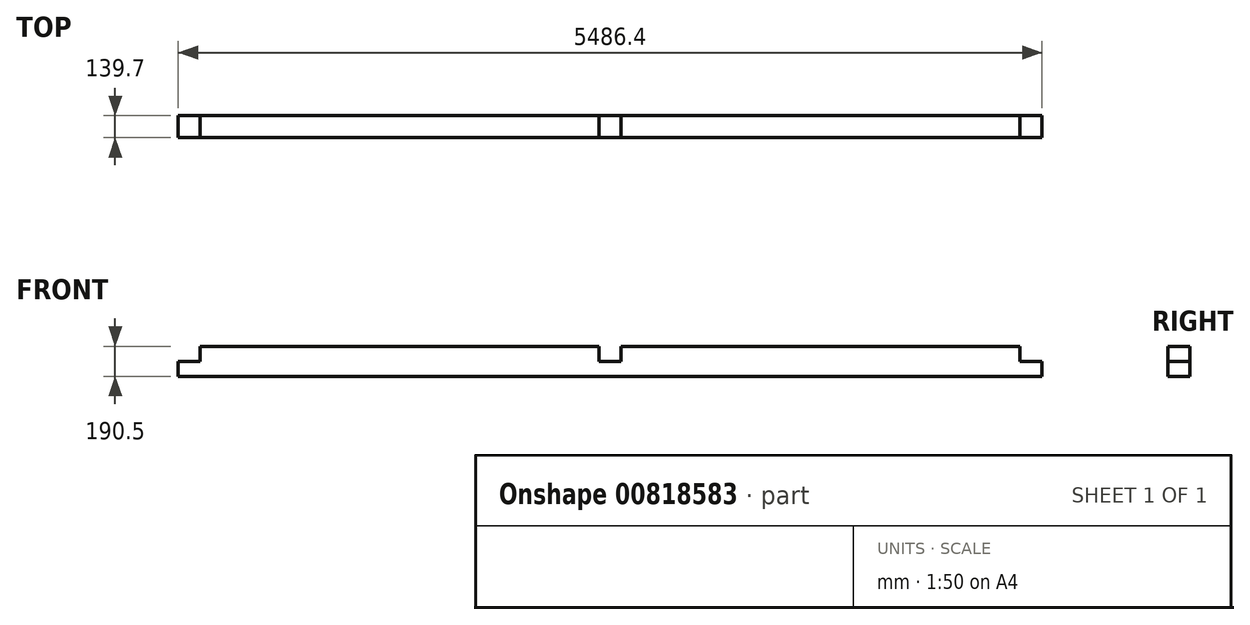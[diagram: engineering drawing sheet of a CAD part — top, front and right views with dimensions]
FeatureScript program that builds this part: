
annotation { "Feature Type Name" : "Feature", "Feature Type Description" : "" }
export const myFeature = defineFeature(function(context is Context, id is Id, definition is map)
    precondition{}
    {
        {
            var Q0;
            Q0=qCreatedBy(makeId("Front.planeOp"),FACE);
            var sketch = newSketch(context, id + "F0", { "sketchPlane" : qUnion([Q0])});
            skLineSegment(sketch, "E0.bottom", {"start": v(181.14, -116.54) * mm, "end": v(2924.34, -116.54) * mm});
            skLineSegment(sketch, "E0.top", {"start": v(181.14, 73.96) * mm, "end": v(5667.54, 73.96) * mm});
            skLineSegment(sketch, "E0.left", {"start": v(181.14, -116.54) * mm, "end": v(181.14, 73.96) * mm});
            skLineSegment(sketch, "E0.right", {"start": v(5667.54, -116.54) * mm, "end": v(5667.54, 73.96) * mm});
            skLineSegment(sketch, "E1.bottom", {"start": v(181.14, 73.96) * mm, "end": v(320.84, 73.96) * mm});
            skLineSegment(sketch, "E1.top", {"start": v(181.14, -21.3) * mm, "end": v(320.84, -21.3) * mm});
            skLineSegment(sketch, "E1.left", {"start": v(181.14, 73.96) * mm, "end": v(181.14, -21.3) * mm});
            skLineSegment(sketch, "E1.right", {"start": v(320.84, 73.96) * mm, "end": v(320.84, -21.3) * mm});
            skLineSegment(sketch, "E2.bottom", {"start": v(2854.5, -21.3) * mm, "end": v(2994.2, -21.3) * mm});
            skLineSegment(sketch, "E2.top", {"start": v(2854.5, 73.96) * mm, "end": v(2994.2, 73.96) * mm});
            skLineSegment(sketch, "E2.left", {"start": v(2854.5, -21.3) * mm, "end": v(2854.5, 73.96) * mm});
            skLineSegment(sketch, "E2.right", {"start": v(2994.2, -21.3) * mm, "end": v(2994.2, 73.96) * mm});
            skLineSegment(sketch, "E3.bottom", {"start": v(5527.84, -21.3) * mm, "end": v(5667.54, -21.3) * mm});
            skLineSegment(sketch, "E3.top", {"start": v(5527.84, 73.96) * mm, "end": v(5667.54, 73.96) * mm});
            skLineSegment(sketch, "E3.left", {"start": v(5527.84, -21.3) * mm, "end": v(5527.84, 73.96) * mm});
            skLineSegment(sketch, "E3.right", {"start": v(5667.54, -21.3) * mm, "end": v(5667.54, 73.96) * mm});
            skLineSegment(sketch, "E4", {"start": v(2924.34, -116.54) * mm, "end": v(5667.54, -116.54) * mm});
            skSolve(sketch);
        }
        {
            var Q0;
            Q0=makeQuery(id+"F0.imprint","IMPRINT",FACE,{"disambiguationData":[TD([[makeQuery(id+"F0.imprint","IMPRINT",EDGE,{"derivedFrom":sQuery(id+"F0.wireOp",EDGE,"E0.bottom")}),1.0]])]});
            extrude(context, id + "F1", {"entities" : qUnion([Q0]), "depth" : 139.7 * mm, "offsetDistance" : 25.4 * mm});
        }
    });
